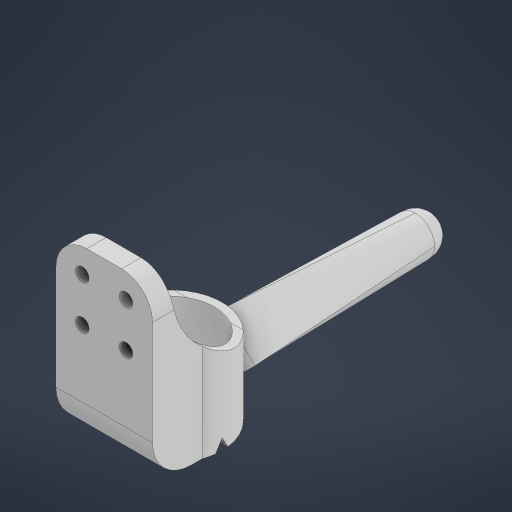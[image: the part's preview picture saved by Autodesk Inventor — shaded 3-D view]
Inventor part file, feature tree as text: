
AUTODESK INVENTOR PART (.ipt)
format: ipt  version: 2023 (Build 270158000, 158)  size: 432,128 bytes
history: native  units: mm
features: sketch x11, extrude x10, plane x4, fillet x4, projected_geometry x2, loft x1, revolve x1, other x1
ambient origin geometry x8: Origin, YZ Plane, XZ Plane, XY Plane, X Axis, Y Axis, Z Axis, Center Point
bodies: Solid1 (feature_tree)
feature tree (34):
  extrude  "Extrusion1"  Depth=2.0mm
  plane  "Work Plane1"
  extrude  "Extrusion2"  Depth=15.5mm
  plane  "Work Plane2"
  extrude  "Extrusion4"  TaperAngle=60.0deg  [1 undecoded]
  sketch  "Sketch7"  dims[d8=3.0mm d9=12.25mm d10=0.0mm]
  extrude  "Extrusion5"  Depth=12.25mm TaperAngle=0.0deg
  extrude  "Extrusion6"  Depth=0.1mm
  fillet  "Fillet1"  Radius=10.25mm
  extrude  "Block Extrusion"  Depth=60.0mm TaperAngle=360.0deg
  extrude  "Extension Extrusion"  Depth=10.0mm TaperAngle=0.0deg
  fillet  "Fillet3"  Radius=5.0mm
  extrude  "Extrusion13"  Depth=10.0mm
  fillet  "Fillet4"  Radius=10.0mm
  extrude  "Extrusion15"  Depth=5.0mm
  plane  "Work Plane6"
  sketch  "Sketch21"  dims[d53=25.0mm d54=0.0mm d55=5.0mm]
  extrude  "Extrusion16"  Depth=16.0mm
  plane  "Work Plane7"
  loft  "Loft2"
  revolve  "Revolution7"  [1 undecoded]
  fillet  "Fillet5"  Radius=10.0mm
  sketch  "Sketch1"  dims[d0=22.5mm d1=2.0mm]
  sketch  "Sketch2"  dims[d2=20.0mm d3=0.0mm d4=15.5mm]
  projected_geometry  "Projected Loop1"
  sketch  "Sketch5"  dims[d5=60.0deg d7=60.0deg]
  sketch  "Sketch12"  dims[d14=-20.25mm d16=0.1mm d18=10.25mm d19=0.0mm]
  sketch  "Sketch16"  dims[d20=6.5mm d21=60.0mm d23=360.0deg]
  sketch  "Sketch18"  dims[d25=3.6mm d26=10.0mm d27=0.0mm d28=5.0mm d29=0.0mm]
  sketch  "Sketch20"  dims[d30=3.0mm d39=25.0mm d40=10.0mm d41=0.0mm]
  projected_geometry  "Projected Loop5"
  sketch  "Sketch22"  dims[d56=22.0mm d57=16.0mm]
  other  "Edges1"
  sketch  "Sketch29"  dims[d58=3.5mm d60=12.0mm d61=18.5mm d62=0.0mm d63=10.0mm d64=8.0mm d69=4.0mm d70=10.0mm d71=6.5mm d72=6.5mm d73=6.5mm d74=6.5mm d75=21.5mm d76=0.0mm d77=12.0mm d78=21.5mm d79=0.0mm d80=-50.0mm d82=0.0mm d83=90.0deg d84=0.0mm d85=90.0deg d96=10.0mm d97=360.0deg d98=10.0mm d51=0.0mm d52=0.0mm]
note: 2 required parameter values undecoded (feature->parameter linkage not recoverable at this tier; creation-order binding heuristic only, values carry confidence <= 0.55)